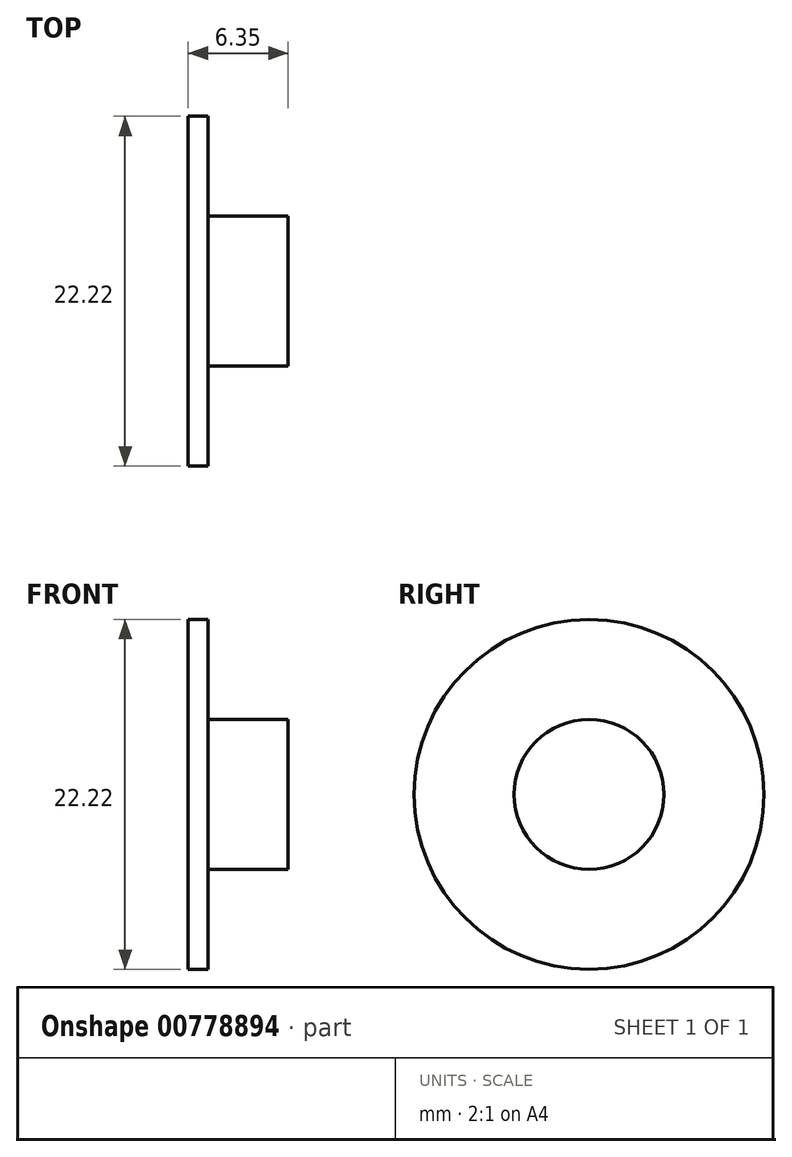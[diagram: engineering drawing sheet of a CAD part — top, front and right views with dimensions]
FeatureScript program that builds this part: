
annotation { "Feature Type Name" : "Feature", "Feature Type Description" : "" }
export const myFeature = defineFeature(function(context is Context, id is Id, definition is map)
    precondition{}
    {
        {
            var Q0;
            Q0=qCreatedBy(makeId("Right.planeOp"),FACE);
            var sketch = newSketch(context, id + "F0", { "sketchPlane" : qUnion([Q0])});
            skCircle(sketch, "E0", {"center": v(0, 0) * mm, "radius": 11.11 * mm});
            skCircle(sketch, "E1", {"center": v(0, 0) * mm, "radius": 4.76 * mm});
            skSolve(sketch);
        }
        {
            var Q0;
            Q0=makeQuery(id+"F0.imprint","IMPRINT",FACE,{"disambiguationData":[TD([[makeQuery(id+"F0.imprint","IMPRINT",EDGE,{"derivedFrom":sQuery(id+"F0.wireOp",EDGE,"E0")}),1.0]])]});
            extrude(context, id + "F1", {"entities" : qUnion([Q0]), "depth" : 1.27 * mm, "offsetDistance" : 25.4 * mm});
        }
        {
            var Q0;
            Q0=makeQuery(id+"F0.imprint","IMPRINT",FACE,{"disambiguationData":[TD([[makeQuery(id+"F0.imprint","IMPRINT",EDGE,{"derivedFrom":sQuery(id+"F0.wireOp",EDGE,"E1")}),1.0]])]});
            extrude(context, id + "F2", {"entities" : qUnion([Q0]), "operationType" : NewBodyOperationType.ADD, "depth" : 6.35 * mm, "offsetDistance" : 25.4 * mm});
        }
    });
